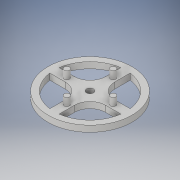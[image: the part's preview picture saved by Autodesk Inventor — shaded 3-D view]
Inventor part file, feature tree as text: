
AUTODESK INVENTOR PART (.ipt)
format: ipt  version: 2019 (Build 230136000, 136)  size: 163,840 bytes
history: native  units: in
note: dims shown in document units (in); Inventor stores cm internally (conversion verified against a paired STEP export)
features: extrude x3, sketch x2
ambient origin geometry x8: Origin, YZ Plane, XZ Plane, XY Plane, X Axis, Y Axis, Z Axis, Center Point
bodies: Body1 (feature_tree)
feature tree (5):
  sketch  "Sketch1"  dims[d1=1.5748in d3=360.0deg d5=0.175in]
  extrude  "Extrusion3"  Depth=0.175in
  extrude  "Extrusion4"  Depth=0.45in
  extrude  "Extrusion5"  Depth=0.2in
  sketch  "Sketch2"  dims[d6=1.5748in d8=360.0deg d10=0.15in d11=0.15in d21=0.2in d22=0.2in d23=0.0in d24=0.45in d25=0.0in d26=0.225in d27=0.45in d28=0.0in]
